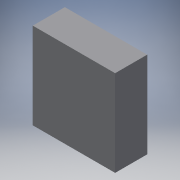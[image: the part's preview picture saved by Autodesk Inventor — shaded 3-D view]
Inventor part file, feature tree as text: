
AUTODESK INVENTOR PART (.ipt)
format: ipt  version: 2018 (Build 220112000, 112)  size: 84,480 bytes
history: native  units: mm
features: extrude x1, sketch x1
ambient origin geometry x8: Origin, YZ Plane, XZ Plane, XY Plane, X Axis, Y Axis, Z Axis, Center Point
bodies: Volumenkörper1 (feature_tree)
feature tree (2):
  extrude  "Extrusion1"  [1 undecoded]
  sketch  "Skizze1"  dims[d0=10.0mm d1=0.0mm]
note: 1 required parameter value undecoded (feature->parameter linkage not recoverable at this tier; creation-order binding heuristic only, values carry confidence <= 0.55)
